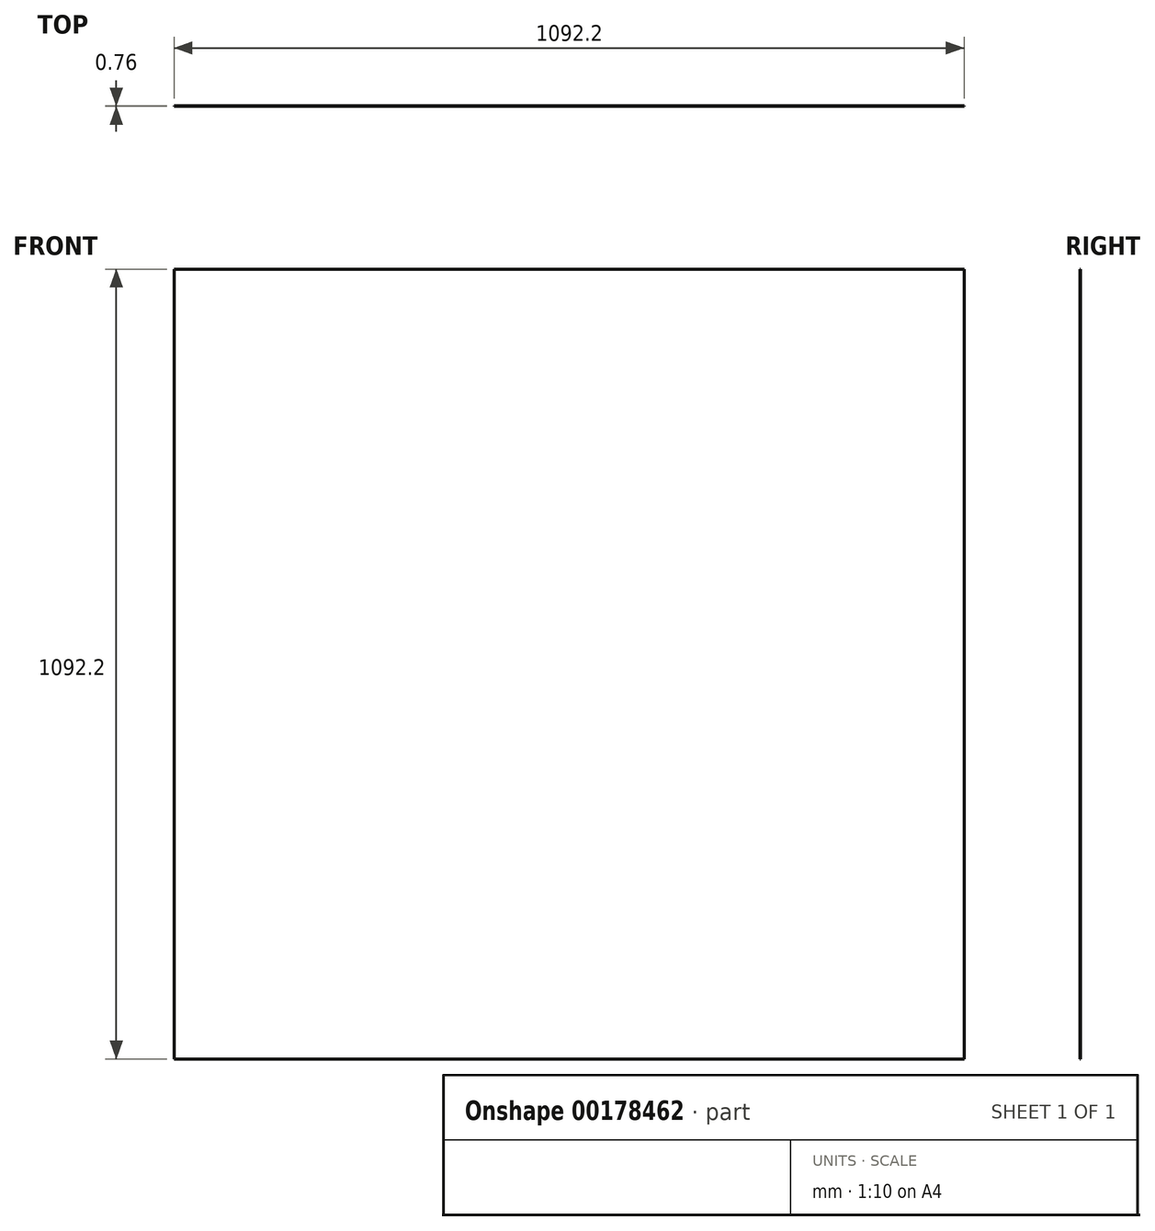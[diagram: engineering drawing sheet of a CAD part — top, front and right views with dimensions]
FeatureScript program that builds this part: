
annotation { "Feature Type Name" : "Feature", "Feature Type Description" : "" }
export const myFeature = defineFeature(function(context is Context, id is Id, definition is map)
    precondition{}
    {
        {
            var Q0;
            Q0=qCreatedBy(makeId("Front.planeOp"),FACE);
            var sketch = newSketch(context, id + "F0", { "sketchPlane" : qUnion([Q0])});
            skLineSegment(sketch, "E0.bottom", {"start": v(546.1, 546.1) * mm, "end": v(-546.1, 546.1) * mm});
            skLineSegment(sketch, "E0.top", {"start": v(546.1, -546.1) * mm, "end": v(-546.1, -546.1) * mm});
            skLineSegment(sketch, "E0.left", {"start": v(546.1, 546.1) * mm, "end": v(546.1, -546.1) * mm});
            skLineSegment(sketch, "E0.right", {"start": v(-546.1, 546.1) * mm, "end": v(-546.1, -546.1) * mm});
            skPoint(sketch, "E0.middle", {"position": v(0, 0) * mm});
            skSolve(sketch);
        }
        {
            var Q0;
            Q0 = qSketchRegion(id + "F0", true);
            extrude(context, id + "F1", {"entities" : qUnion([Q0]), "depth" : 0.76 * mm});
        }
    });
